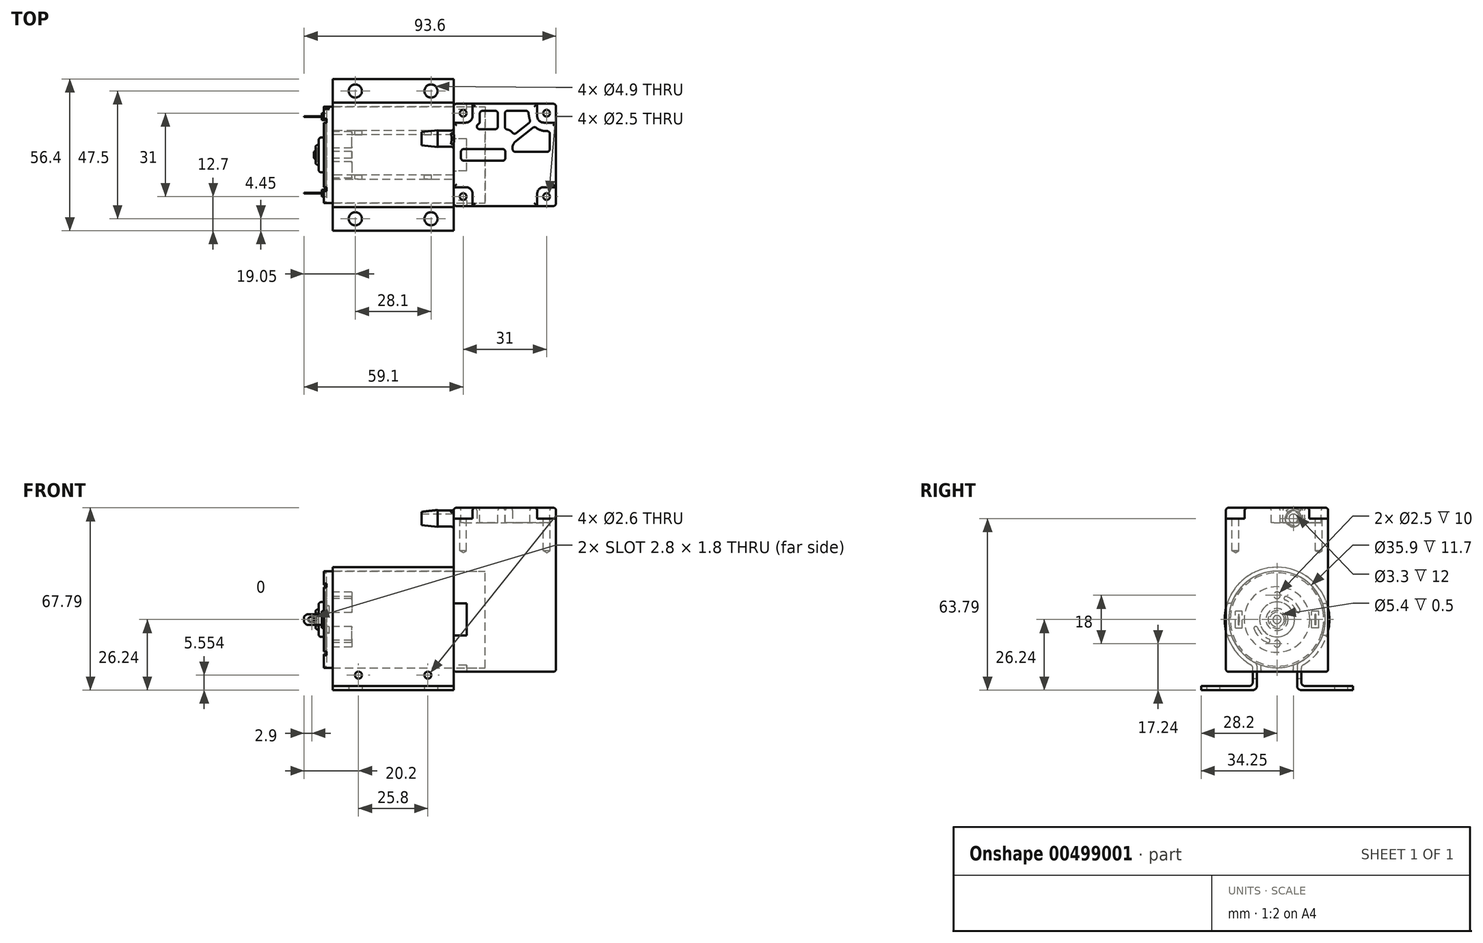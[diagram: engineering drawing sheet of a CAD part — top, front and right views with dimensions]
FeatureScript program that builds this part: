
annotation { "Feature Type Name" : "Feature", "Feature Type Description" : "" }
export const myFeature = defineFeature(function(context is Context, id is Id, definition is map)
    precondition{}
    {
        {
            var Q0;
            Q0=qCreatedBy(makeId("Front.planeOp"),FACE);
            var sketch = newSketch(context, id + "F0", { "sketchPlane" : qUnion([Q0])});
            skLineSegment(sketch, "E0", {"start": v(-59, 17.35) * mm, "end": v(-60, 17.35) * mm});
            skLineSegment(sketch, "E1", {"start": v(-60, 17.35) * mm, "end": v(-60, 17.95) * mm});
            skLineSegment(sketch, "E2", {"start": v(-60, 17.95) * mm, "end": v(0, 17.95) * mm});
            skLineSegment(sketch, "E3", {"start": v(0, 0) * mm, "end": v(0, 17.95) * mm});
            skLineSegment(sketch, "E4", {"start": v(0, 0) * mm, "end": v(-63.6, 0) * mm});
            skLineSegment(sketch, "E5", {"start": v(-61.9, 6.5) * mm, "end": v(-61.9, 4.1) * mm});
            skLineSegment(sketch, "E6", {"start": v(-63, 3.3) * mm, "end": v(-63, 2.7) * mm});
            skLineSegment(sketch, "E7", {"start": v(-63, 2.7) * mm, "end": v(-62.5, 2.7) * mm});
            skLineSegment(sketch, "E8", {"start": v(-62.5, 2.7) * mm, "end": v(-62.5, 1.5) * mm});
            skLineSegment(sketch, "E9", {"start": v(-62.5, 1.5) * mm, "end": v(-63.6, 1.5) * mm});
            skLineSegment(sketch, "E10", {"start": v(-63.6, 1.5) * mm, "end": v(-63.6, 0) * mm});
            skLineSegment(sketch, "E11", {"start": v(-61.9, 6.5) * mm, "end": v(-59.5, 6.5) * mm});
            skLineSegment(sketch, "E12", {"start": v(-59.5, 6.5) * mm, "end": v(-59.5, 12.2) * mm});
            skLineSegment(sketch, "E13", {"start": v(-59, 17.35) * mm, "end": v(-59, 12.2) * mm});
            skLineSegment(sketch, "E14", {"start": v(-59, 12.2) * mm, "end": v(-59.5, 12.2) * mm});
            skPoint(sketch, "E15", {"position": v(-61.9, 5.3) * mm});
            skLineSegment(sketch, "E16", {"start": v(-61.9, 4.1) * mm, "end": v(-63, 3.3) * mm});
            skSolve(sketch);
        }
        {
            var Q0;
            Q0 = qSketchRegion(id + "F0", true);
            var Q1;
            Q1=sQuery(id+"F0.wireOp",EDGE,"E4");
            revolve(context, id + "F1", {"entities" : qUnion([Q0]), "axis" : qUnion([Q1]), "revolveType" : RevolveType.FULL});
        }
        {
            var Q0;
            Q0=makeQuery(id+"F1.opRevolve","SWEPT_EDGE",EDGE,{"disambiguationData":[OSD([sQuery(id+"F0.wireOp",EDGE,"E12"),sQuery(id+"F0.wireOp",EDGE,"E14")])]});
            var Q1;
            Q1=makeQuery(id+"F1.opRevolve","SWEPT_EDGE",EDGE,{"disambiguationData":[OSD([sQuery(id+"F0.wireOp",EDGE,"E9"),sQuery(id+"F0.wireOp",EDGE,"E10")])]});
            fillet(context, id + "F2", {"entities" : qUnion([Q0, Q1]), "radius" : 0.5 * mm, "tangentPropagation" : true, "allowEdgeOverflow" : false});
        }
        {
            var Q0;
            Q0=makeQuery(id+"F1.opRevolve","SWEPT_EDGE",EDGE,{"disambiguationData":[OSD([sQuery(id+"F0.wireOp",EDGE,"E5"),sQuery(id+"F0.wireOp",EDGE,"E11")])]});
            fillet(context, id + "F3", {"entities" : qUnion([Q0]), "radius" : 1 * mm, "tangentPropagation" : true, "allowEdgeOverflow" : false});
        }
        {
            var Q0;
            Q0=makeQuery(id+"F1.opRevolve","SWEPT_FACE",FACE,{"disambiguationData":[OSD([sQuery(id+"F0.wireOp",EDGE,"E12")])]});
            var sketch = newSketch(context, id + "F4", { "sketchPlane" : qUnion([Q0])});
            skArc(sketch, "E17", {"start": v(-3.56, 8.54) * mm, "mid": v(-6.54, 6.54) * mm, "end": v(-8.54, 3.56) * mm});
            skArc(sketch, "E18", {"start": v(-3.02, 7.24) * mm, "mid": v(-5.55, 5.55) * mm, "end": v(-7.24, 3.02) * mm});
            skArc(sketch, "E19", {"start": v(-8.54, 3.56) * mm, "mid": v(-8.16, 2.65) * mm, "end": v(-7.24, 3.02) * mm});
            skArc(sketch, "E20", {"start": v(-3.02, 7.24) * mm, "mid": v(-2.65, 8.16) * mm, "end": v(-3.56, 8.54) * mm});
            skLineSegment(sketch, "E21", {"start": v(0, 9) * mm, "end": v(0, 0) * mm, "construction": true});
            skLineSegment(sketch, "E22", {"start": v(0, 0) * mm, "end": v(0, -9) * mm, "construction": true});
            skCircle(sketch, "E23", {"center": v(0, 9) * mm, "radius": 1.25 * mm});
            skCircle(sketch, "E24", {"center": v(0, -9) * mm, "radius": 1.25 * mm});
            skLineSegment(sketch, "E25", {"start": v(0, 0) * mm, "end": v(-9.9, 9.9) * mm, "construction": true});
            skArc(sketch, "E26.1.0", {"start": v(3.02, -7.24) * mm, "mid": v(5.55, -5.55) * mm, "end": v(7.24, -3.02) * mm});
            skArc(sketch, "E26.1.1", {"start": v(3.56, -8.54) * mm, "mid": v(6.54, -6.54) * mm, "end": v(8.54, -3.56) * mm});
            skArc(sketch, "E26.1.2", {"start": v(3.02, -7.24) * mm, "mid": v(2.65, -8.16) * mm, "end": v(3.56, -8.54) * mm});
            skArc(sketch, "E26.1.3", {"start": v(8.54, -3.56) * mm, "mid": v(8.16, -2.65) * mm, "end": v(7.24, -3.02) * mm});
            skSolve(sketch);
        }
        {
            var Q0;
            Q0=qSketchRegion(id+"F4",true);
            extrude(context, id + "F5", {"entities" : qUnion([Q0]), "operationType" : NewBodyOperationType.REMOVE, "oppositeDirection" : true, "depth" : 10 * mm});
        }
        {
            var Q0;
            Q0=makeQuery(id+"F1.opRevolve","SWEPT_FACE",FACE,{"disambiguationData":[OSD([sQuery(id+"F0.wireOp",EDGE,"E1")])]});
            var sketch = newSketch(context, id + "F6", { "sketchPlane" : qUnion([Q0])});
            skArc(sketch, "E27.0", {"start": v(-11.6, 12.9) * mm, "mid": v(-12.3, 12.24) * mm, "end": v(-12.96, 11.53) * mm});
            skArc(sketch, "E28.0", {"start": v(-12, 13.35) * mm, "mid": v(-12.73, 12.66) * mm, "end": v(-13.41, 11.93) * mm});
            skLineSegment(sketch, "E29", {"start": v(-13.41, 11.93) * mm, "end": v(-12.96, 11.53) * mm});
            skLineSegment(sketch, "E30", {"start": v(-12, 13.35) * mm, "end": v(-11.6, 12.9) * mm});
            skLineSegment(sketch, "E31.MirrorCS", {"start": v(12, 13.35) * mm, "end": v(11.6, 12.9) * mm});
            skLineSegment(sketch, "E32.MirrorCS", {"start": v(13.41, 11.93) * mm, "end": v(12.96, 11.53) * mm});
            skLineSegment(sketch, "E33.MirrorCS", {"start": v(-13.41, -11.93) * mm, "end": v(-12.96, -11.53) * mm});
            skLineSegment(sketch, "E34.MirrorCS", {"start": v(-12, -13.35) * mm, "end": v(-11.6, -12.9) * mm});
            skLineSegment(sketch, "E35.MirrorCS", {"start": v(13.41, -11.93) * mm, "end": v(12.96, -11.53) * mm});
            skLineSegment(sketch, "E36.MirrorCS", {"start": v(12, -13.35) * mm, "end": v(11.6, -12.9) * mm});
            skArc(sketch, "E37.trimOffspring", {"start": v(-12.96, -11.53) * mm, "mid": v(-12.3, -12.24) * mm, "end": v(-11.6, -12.9) * mm});
            skArc(sketch, "E38.trimOffspring", {"start": v(-13.41, -11.93) * mm, "mid": v(-12.73, -12.66) * mm, "end": v(-12, -13.35) * mm});
            skArc(sketch, "E39.trimOffspring", {"start": v(12.96, 11.53) * mm, "mid": v(12.3, 12.24) * mm, "end": v(11.6, 12.9) * mm});
            skArc(sketch, "E40.trimOffspring", {"start": v(13.41, 11.93) * mm, "mid": v(12.73, 12.66) * mm, "end": v(12, 13.35) * mm});
            skArc(sketch, "E41.trimOffspring", {"start": v(12, -13.35) * mm, "mid": v(12.73, -12.66) * mm, "end": v(13.41, -11.93) * mm});
            skArc(sketch, "E42.trimOffspring", {"start": v(11.6, -12.9) * mm, "mid": v(12.3, -12.24) * mm, "end": v(12.96, -11.53) * mm});
            skLineSegment(sketch, "E43", {"start": v(-17.92, 1) * mm, "end": v(-17.32, 0.97) * mm});
            skLineSegment(sketch, "E44", {"start": v(-17.92, -1) * mm, "end": v(-17.32, -0.97) * mm});
            skArc(sketch, "E45.0", {"start": v(-17.32, 0.97) * mm, "mid": v(-17.35, 0) * mm, "end": v(-17.32, -0.97) * mm});
            skArc(sketch, "E46.0", {"start": v(-17.92, 1) * mm, "mid": v(-17.95, 0) * mm, "end": v(-17.92, -1) * mm});
            skSolve(sketch);
        }
        {
            var Q0;
            Q0=qSketchRegion(id+"F6",true);
            var Q1;
            Q1=makeQuery(id+"F1.opRevolve","SWEPT_FACE",FACE,{"disambiguationData":[OSD([sQuery(id+"F0.wireOp",EDGE,"E13")])]});
            extrude(context, id + "F7", {"entities" : qUnion([Q0]), "operationType" : NewBodyOperationType.REMOVE, "endBound" : BoundingType.UP_TO_SURFACE, "oppositeDirection" : true, "endBoundEntityFace" : qUnion([Q1]), "depth" : 25 * mm});
        }
        {
            var Q0;
            Q0=makeQuery(id+"F7.boolean.opBoolean","SPLIT",FACE,{"disambiguationData":[TD([makeQuery(id+"F7.opExtrude","SWEPT_FACE",FACE,{"disambiguationData":[OSD([sQuery(id+"F6.wireOp",EDGE,"E32.MirrorCS")])]})])],"derivedFrom":makeQuery(id+"F1.opRevolve","SWEPT_FACE",FACE,{"disambiguationData":[OSD([sQuery(id+"F0.wireOp",EDGE,"E1")])]})});
            var sketch = newSketch(context, id + "F8", { "sketchPlane" : qUnion([Q0])});
            skLineSegment(sketch, "E47", {"start": v(-17.2, 5.13) * mm, "end": v(-16.63, 4.96) * mm});
            skLineSegment(sketch, "E48", {"start": v(-17.75, 2.7) * mm, "end": v(-17.15, 2.6) * mm});
            skArc(sketch, "E49.0", {"start": v(-17.15, 2.6) * mm, "mid": v(-16.93, 3.79) * mm, "end": v(-16.63, 4.96) * mm});
            skArc(sketch, "E50.0", {"start": v(-17.75, 2.7) * mm, "mid": v(-17.52, 3.92) * mm, "end": v(-17.2, 5.13) * mm});
            skPoint(sketch, "E51.orphan", {"position": v(-17.92, 1) * mm});
            skArc(sketch, "E52.MirrorCS", {"start": v(-17.15, -2.6) * mm, "mid": v(-16.93, -3.79) * mm, "end": v(-16.63, -4.96) * mm});
            skLineSegment(sketch, "E53.MirrorCS", {"start": v(-17.2, -5.13) * mm, "end": v(-16.63, -4.96) * mm});
            skArc(sketch, "E54.MirrorCS", {"start": v(-17.75, -2.7) * mm, "mid": v(-17.52, -3.92) * mm, "end": v(-17.2, -5.13) * mm});
            skLineSegment(sketch, "E55.MirrorCS", {"start": v(-17.75, -2.7) * mm, "end": v(-17.15, -2.6) * mm});
            skSolve(sketch);
        }
        {
            var Q0;
            Q0=qSketchRegion(id+"F8",true);
            extrude(context, id + "F9", {"entities" : qUnion([Q0]), "operationType" : NewBodyOperationType.REMOVE, "oppositeDirection" : true, "depth" : 2 * mm});
        }
        {
            var Q0;
            {var subQ0=sQuery(id+"F0.wireOp",EDGE,"E13");Q0=makeQuery(id+"F7.boolean.opBoolean","MERGE",FACE,{"derivedFrom":[makeQuery(id+"F1.opRevolve","SWEPT_FACE",FACE,{"disambiguationData":[OSD([subQ0])]}),makeQuery(id+"F7.opExtrude","CAP_FACE",FACE,{"disambiguationData":[OSD([subQ0]),ownerDisambiguation([makeQuery(id+"F6.imprint","IMPRINT",EDGE,{"derivedFrom":sQuery(id+"F6.wireOp",EDGE,"E27.0")})])],"isStart":false}),makeQuery(id+"F7.opExtrude","CAP_FACE",FACE,{"disambiguationData":[OSD([subQ0]),ownerDisambiguation([makeQuery(id+"F6.imprint","IMPRINT",EDGE,{"derivedFrom":sQuery(id+"F6.wireOp",EDGE,"E31.MirrorCS")})])],"isStart":false}),makeQuery(id+"F7.opExtrude","CAP_FACE",FACE,{"disambiguationData":[OSD([subQ0]),ownerDisambiguation([makeQuery(id+"F6.imprint","IMPRINT",EDGE,{"derivedFrom":sQuery(id+"F6.wireOp",EDGE,"E33.MirrorCS")})])],"isStart":false}),makeQuery(id+"F7.opExtrude","CAP_FACE",FACE,{"disambiguationData":[OSD([subQ0]),ownerDisambiguation([makeQuery(id+"F6.imprint","IMPRINT",EDGE,{"derivedFrom":sQuery(id+"F6.wireOp",EDGE,"E35.MirrorCS")})])],"isStart":false}),makeQuery(id+"F7.opExtrude","CAP_FACE",FACE,{"disambiguationData":[OSD([subQ0]),ownerDisambiguation([makeQuery(id+"F6.imprint","IMPRINT",EDGE,{"derivedFrom":sQuery(id+"F6.wireOp",EDGE,"E43")})])],"isStart":false})]});}
            var sketch = newSketch(context, id + "F10", { "sketchPlane" : qUnion([Q0])});
            skLineSegment(sketch, "E56.left", {"start": v(-12.9, -3.1) * mm, "end": v(-12.9, 3.1) * mm});
            skLineSegment(sketch, "E56.right", {"start": v(-15.5, -3.1) * mm, "end": v(-15.5, 3.1) * mm});
            skPoint(sketch, "E56.middle", {"position": v(-14.2, 0) * mm});
            skLineSegment(sketch, "E57.MirrorCS", {"start": v(12.9, -3.1) * mm, "end": v(12.9, 3.1) * mm});
            skLineSegment(sketch, "E58.MirrorCS", {"start": v(15.5, -3.1) * mm, "end": v(15.5, 3.1) * mm});
            skLineSegment(sketch, "E59", {"start": v(-15.5, 3.1) * mm, "end": v(-12.9, 3.1) * mm});
            skLineSegment(sketch, "E60", {"start": v(-15.5, -3.1) * mm, "end": v(-12.9, -3.1) * mm});
            skLineSegment(sketch, "E61", {"start": v(12.9, 3.1) * mm, "end": v(15.5, 3.1) * mm});
            skLineSegment(sketch, "E62", {"start": v(15.5, -3.1) * mm, "end": v(12.9, -3.1) * mm});
            skSolve(sketch);
        }
        {
            var Q0;
            Q0=qSketchRegion(id+"F10",true);
            extrude(context, id + "F11", {"entities" : qUnion([Q0]), "operationType" : NewBodyOperationType.ADD, "depth" : 1.7 * mm});
        }
        {
            var Q0;
            Q0=makeQuery(id+"F11.opExtrude","SWEPT_FACE",FACE,{"disambiguationData":[OSD([sQuery(id+"F10.wireOp",EDGE,"E56.right")])]});
            var Q1;
            Q1=makeQuery(id+"F11.opExtrude","SWEPT_FACE",FACE,{"disambiguationData":[OSD([sQuery(id+"F10.wireOp",EDGE,"E56.left")])]});
            cPlane(context, id + "F12", {"entities" : qUnion([Q0, Q1]), "cplaneType" : CPlaneType.MID_PLANE, "offset" : 25 * mm, "width" : 150 * mm, "height" : 150 * mm});
        }
        {
            var Q0;
            Q0=qCreatedBy(id+"F12.planeOp",FACE);
            var sketch = newSketch(context, id + "F13", { "sketchPlane" : qUnion([Q0])});
            skLineSegment(sketch, "E63", {"start": v(67.3, -2) * mm, "end": v(60.7, -2) * mm});
            skLineSegment(sketch, "E64", {"start": v(60.7, -2) * mm, "end": v(60.7, 2) * mm});
            skLineSegment(sketch, "E65", {"start": v(60.7, 2) * mm, "end": v(67.3, 2) * mm});
            skLineSegment(sketch, "E66", {"start": v(67.3, 2) * mm, "end": v(67.3, -2) * mm});
            skArc(sketch, "E67", {"start": v(64.9, -0.9) * mm, "mid": v(65.8, 0) * mm, "end": v(64.9, 0.9) * mm});
            skPoint(sketch, "E67.centerSnap0", {"position": v(60.7, 0) * mm});
            skArc(sketch, "E68", {"start": v(63.9, 0.9) * mm, "mid": v(63, 0) * mm, "end": v(63.9, -0.9) * mm});
            skLineSegment(sketch, "E69", {"start": v(64.9, 0.9) * mm, "end": v(63.9, 0.9) * mm});
            skLineSegment(sketch, "E70", {"start": v(64.9, -0.9) * mm, "end": v(63.9, -0.9) * mm});
            skSolve(sketch);
        }
        {
            var Q0;
            Q0=qSketchRegion(id+"F13",true);
            extrude(context, id + "F14", {"entities" : qUnion([Q0]), "endBound" : BoundingType.SYMMETRIC, "depth" : 0.3 * mm});
        }
        {
            var Q0;
            Q0=makeQuery(id+"F14.opExtrude","SWEPT_EDGE",EDGE,{"disambiguationData":[OSD([sQuery(id+"F13.wireOp",EDGE,"E65"),sQuery(id+"F13.wireOp",EDGE,"E66")])]});
            var Q1;
            Q1=makeQuery(id+"F14.opExtrude","SWEPT_EDGE",EDGE,{"disambiguationData":[OSD([sQuery(id+"F13.wireOp",EDGE,"E63"),sQuery(id+"F13.wireOp",EDGE,"E66")])]});
            chamfer(context, id + "F15", {"entities" : qUnion([Q0, Q1]), "width" : 1 * mm, "tangentPropagation" : true});
        }
        {
            var Q0;
            Q0=makeQuery(id+"F14.opExtrude","SWEPT_BODY",BODY,{"disambiguationData":[OSD([sQuery(id+"F13.wireOp",EDGE,"E63"),sQuery(id+"F13.wireOp",EDGE,"E64"),sQuery(id+"F13.wireOp",EDGE,"E65"),sQuery(id+"F13.wireOp",EDGE,"E66"),sQuery(id+"F13.wireOp",EDGE,"E67"),sQuery(id+"F13.wireOp",EDGE,"E68"),sQuery(id+"F13.wireOp",EDGE,"E69"),sQuery(id+"F13.wireOp",EDGE,"E70")])]});
            var Q1;
            Q1=qCreatedBy(makeId("Front.planeOp"),FACE);
            mirror(context, id + "F16", {"operationType" : NewBodyOperationType.ADD, "entities" : qUnion([Q0]), "mirrorPlane" : qUnion([Q1])});
        }
        {
            var Q0;
            Q0=makeQuery(id+"F7.boolean.opBoolean","SPLIT",FACE,{"disambiguationData":[TD([makeQuery(id+"F7.opExtrude","SWEPT_FACE",FACE,{"disambiguationData":[OSD([sQuery(id+"F6.wireOp",EDGE,"E30")])]})])],"derivedFrom":makeQuery(id+"F1.opRevolve","SWEPT_FACE",FACE,{"disambiguationData":[OSD([sQuery(id+"F0.wireOp",EDGE,"E1")])]})});
            cPlane(context, id + "F17", {"entities" : qUnion([Q0]), "cplaneType" : CPlaneType.OFFSET, "offset" : 3.3 * mm, "oppositeDirection" : true, "width" : 150 * mm, "height" : 150 * mm});
        }
        {
            var Q0;
            Q0=qCreatedBy(id+"F17.planeOp",FACE);
            var sketch = newSketch(context, id + "F18", { "sketchPlane" : qUnion([Q0])});
            skArc(sketch, "E71", {"start": v(7.5, -16.3) * mm, "mid": v(0, 17.95) * mm, "end": v(-7.5, -16.3) * mm});
            skLineSegment(sketch, "E72", {"start": v(-7.5, -16.3) * mm, "end": v(-7.5, -26.24) * mm});
            skLineSegment(sketch, "E73", {"start": v(-7.5, -26.24) * mm, "end": v(-28.2, -26.24) * mm});
            skLineSegment(sketch, "E74", {"start": v(-28.2, -26.24) * mm, "end": v(-28.2, -24.74) * mm});
            skLineSegment(sketch, "E75", {"start": v(-28.2, -24.74) * mm, "end": v(-9, -24.74) * mm});
            skLineSegment(sketch, "E76", {"start": v(-9, -24.74) * mm, "end": v(-9, -17.24) * mm});
            skLineSegment(sketch, "E77.MirrorCS", {"start": v(7.5, -16.3) * mm, "end": v(7.5, -26.24) * mm});
            skLineSegment(sketch, "E78.MirrorCS", {"start": v(9, -24.74) * mm, "end": v(9, -17.24) * mm});
            skLineSegment(sketch, "E79.MirrorCS", {"start": v(28.2, -24.74) * mm, "end": v(9, -24.74) * mm});
            skLineSegment(sketch, "E80.MirrorCS", {"start": v(7.5, -26.24) * mm, "end": v(28.2, -26.24) * mm});
            skLineSegment(sketch, "E81.MirrorCS", {"start": v(28.2, -26.24) * mm, "end": v(28.2, -24.74) * mm});
            skArc(sketch, "E82.trimOffspring", {"start": v(9, -17.24) * mm, "mid": v(0, 19.45) * mm, "end": v(-9, -17.24) * mm});
            skSolve(sketch);
        }
        {
            var Q0;
            Q0=makeQuery(id+"F18.imprint","IMPRINT",FACE,{"disambiguationData":[TD([[makeQuery(id+"F18.imprint","IMPRINT",EDGE,{"derivedFrom":sQuery(id+"F18.wireOp",EDGE,"E71")}),-1.0]])]});
            extrude(context, id + "F19", {"entities" : qUnion([Q0]), "oppositeDirection" : true, "depth" : 45 * mm});
        }
        {
            var Q0;
            Q0=makeQuery(id+"F19.opExtrude","SWEPT_EDGE",EDGE,{"disambiguationData":[OSD([sQuery(id+"F18.wireOp",EDGE,"E76"),sQuery(id+"F18.wireOp",EDGE,"E82.trimOffspring")])]});
            var Q1;
            Q1=makeQuery(id+"F19.opExtrude","SWEPT_EDGE",EDGE,{"disambiguationData":[OSD([sQuery(id+"F18.wireOp",EDGE,"E75"),sQuery(id+"F18.wireOp",EDGE,"E76")])]});
            var Q2;
            Q2=makeQuery(id+"F19.opExtrude","SWEPT_EDGE",EDGE,{"disambiguationData":[OSD([sQuery(id+"F18.wireOp",EDGE,"E72"),sQuery(id+"F18.wireOp",EDGE,"E73")])]});
            var Q3;
            Q3=makeQuery(id+"F19.opExtrude","SWEPT_EDGE",EDGE,{"disambiguationData":[OSD([sQuery(id+"F18.wireOp",EDGE,"E71"),sQuery(id+"F18.wireOp",EDGE,"E72")])]});
            var Q4;
            Q4=makeQuery(id+"F19.opExtrude","SWEPT_EDGE",EDGE,{"disambiguationData":[OSD([sQuery(id+"F18.wireOp",EDGE,"E71"),sQuery(id+"F18.wireOp",EDGE,"E77.MirrorCS")])]});
            var Q5;
            Q5=makeQuery(id+"F19.opExtrude","SWEPT_EDGE",EDGE,{"disambiguationData":[OSD([sQuery(id+"F18.wireOp",EDGE,"E77.MirrorCS"),sQuery(id+"F18.wireOp",EDGE,"E80.MirrorCS")])]});
            var Q6;
            Q6=makeQuery(id+"F19.opExtrude","SWEPT_EDGE",EDGE,{"disambiguationData":[OSD([sQuery(id+"F18.wireOp",EDGE,"E78.MirrorCS"),sQuery(id+"F18.wireOp",EDGE,"E79.MirrorCS")])]});
            var Q7;
            Q7=makeQuery(id+"F19.opExtrude","SWEPT_EDGE",EDGE,{"disambiguationData":[OSD([sQuery(id+"F18.wireOp",EDGE,"E78.MirrorCS"),sQuery(id+"F18.wireOp",EDGE,"E82.trimOffspring")])]});
            fillet(context, id + "F20", {"entities" : qUnion([Q0, Q1, Q2, Q3, Q4, Q5, Q6, Q7]), "radius" : 1.5 * mm, "tangentPropagation" : true, "allowEdgeOverflow" : false});
        }
        {
            var Q0;
            Q0=qCreatedBy(makeId("Front.planeOp"),FACE);
            var sketch = newSketch(context, id + "F21", { "sketchPlane" : qUnion([Q0])});
            skLineSegment(sketch, "E83.bottom", {"start": v(-11.7, 41.55) * mm, "end": v(26.3, 41.55) * mm});
            skLineSegment(sketch, "E83.top", {"start": v(-11.7, -19.45) * mm, "end": v(26.3, -19.45) * mm});
            skLineSegment(sketch, "E83.left", {"start": v(-11.7, 41.55) * mm, "end": v(-11.7, -19.45) * mm});
            skLineSegment(sketch, "E83.right", {"start": v(26.3, 41.55) * mm, "end": v(26.3, -19.45) * mm});
            skLineSegment(sketch, "E84", {"start": v(0, -17.95) * mm, "end": v(-60, -17.95) * mm, "construction": true});
            skLineSegment(sketch, "E85", {"start": v(-60, 17.95) * mm, "end": v(0, 17.95) * mm, "construction": true});
            skSolve(sketch);
        }
        {
            var Q0;
            Q0=makeQuery(id+"F21.imprint","IMPRINT",FACE,{"disambiguationData":[TD([[makeQuery(id+"F21.imprint","IMPRINT",EDGE,{"derivedFrom":sQuery(id+"F21.wireOp",EDGE,"E83.bottom")}),-1.0]])]});
            extrude(context, id + "F22", {"entities" : qUnion([Q0]), "endBound" : BoundingType.SYMMETRIC, "depth" : 38 * mm});
        }
        {
            var Q0;
            Q0=makeQuery(id+"F1.opRevolve","SWEPT_BODY",BODY,{"disambiguationData":[OSD([sQuery(id+"F0.wireOp",EDGE,"E0"),sQuery(id+"F0.wireOp",EDGE,"E1"),sQuery(id+"F0.wireOp",EDGE,"E2"),sQuery(id+"F0.wireOp",EDGE,"E3"),sQuery(id+"F0.wireOp",EDGE,"E4"),sQuery(id+"F0.wireOp",EDGE,"E5"),sQuery(id+"F0.wireOp",EDGE,"E6"),sQuery(id+"F0.wireOp",EDGE,"E7"),sQuery(id+"F0.wireOp",EDGE,"E8"),sQuery(id+"F0.wireOp",EDGE,"E9"),sQuery(id+"F0.wireOp",EDGE,"E10"),sQuery(id+"F0.wireOp",EDGE,"E11"),sQuery(id+"F0.wireOp",EDGE,"E12"),sQuery(id+"F0.wireOp",EDGE,"E13"),sQuery(id+"F0.wireOp",EDGE,"E14"),sQuery(id+"F0.wireOp",EDGE,"E16")])]});
            var Q1;
            Q1=makeQuery(id+"F22.opExtrude","SWEPT_BODY",BODY,{"disambiguationData":[OSD([sQuery(id+"F21.wireOp",EDGE,"E83.bottom"),sQuery(id+"F21.wireOp",EDGE,"E83.top"),sQuery(id+"F21.wireOp",EDGE,"E83.left"),sQuery(id+"F21.wireOp",EDGE,"E83.right")])]});
            booleanBodies(context, id + "F23", {"operationType" : BooleanOperationType.SUBTRACTION, "tools" : qUnion([Q0]), "targets" : qUnion([Q1]), "keepTools" : true});
        }
        {
            var Q0;
            Q0=makeQuery(id+"F22.opExtrude","SWEPT_FACE",FACE,{"disambiguationData":[OSD([sQuery(id+"F21.wireOp",EDGE,"E83.left")])]});
            var sketch = newSketch(context, id + "F24", { "sketchPlane" : qUnion([Q0])});
            skArc(sketch, "E86", {"start": v(-16.94, -5.95) * mm, "mid": v(-17.95, 0) * mm, "end": v(-16.94, 5.95) * mm});
            skLineSegment(sketch, "E87", {"start": v(-16.94, 5.95) * mm, "end": v(-19, 5.95) * mm});
            skLineSegment(sketch, "E88", {"start": v(-19, 5.95) * mm, "end": v(-19, -5.95) * mm});
            skLineSegment(sketch, "E89", {"start": v(-19, -5.95) * mm, "end": v(-16.94, -5.95) * mm});
            skLineSegment(sketch, "E90.MirrorCS", {"start": v(16.94, 5.95) * mm, "end": v(19, 5.95) * mm});
            skLineSegment(sketch, "E91.MirrorCS", {"start": v(19, 5.95) * mm, "end": v(19, -5.95) * mm});
            skLineSegment(sketch, "E92.MirrorCS", {"start": v(19, -5.95) * mm, "end": v(16.94, -5.95) * mm});
            skArc(sketch, "E93.MirrorCS", {"start": v(16.94, -5.95) * mm, "mid": v(17.95, 0) * mm, "end": v(16.94, 5.95) * mm});
            skLineSegment(sketch, "E94", {"start": v(-5.95, -16.94) * mm, "end": v(-5.95, -19.45) * mm});
            skLineSegment(sketch, "E95", {"start": v(-5.95, -19.45) * mm, "end": v(5.95, -19.45) * mm});
            skLineSegment(sketch, "E96", {"start": v(5.95, -19.45) * mm, "end": v(5.95, -16.94) * mm});
            skArc(sketch, "E97.trimOffspring", {"start": v(5.95, -16.94) * mm, "mid": v(0, -17.95) * mm, "end": v(-5.95, -16.94) * mm});
            skSolve(sketch);
        }
        {
            var Q0;
            Q0=makeQuery(id+"F24.imprint","IMPRINT",FACE,{"disambiguationData":[TD([[makeQuery(id+"F24.imprint","IMPRINT",EDGE,{"derivedFrom":sQuery(id+"F24.wireOp",EDGE,"E90.MirrorCS")}),-1.0]])]});
            var Q1;
            Q1=makeQuery(id+"F24.imprint","IMPRINT",FACE,{"disambiguationData":[TD([[makeQuery(id+"F24.imprint","IMPRINT",EDGE,{"derivedFrom":sQuery(id+"F24.wireOp",EDGE,"E86")}),-1.0]])]});
            var Q2;
            Q2=makeQuery(id+"F24.imprint","IMPRINT",FACE,{"disambiguationData":[TD([[makeQuery(id+"F24.imprint","IMPRINT",EDGE,{"derivedFrom":sQuery(id+"F24.wireOp",EDGE,"E94")}),1.0]])]});
            extrude(context, id + "F25", {"entities" : qUnion([Q0, Q1, Q2]), "operationType" : NewBodyOperationType.REMOVE, "oppositeDirection" : true, "depth" : 4.8 * mm});
        }
        {
            var Q0;
            Q0=makeQuery(id+"F22.opExtrude","SWEPT_FACE",FACE,{"disambiguationData":[OSD([sQuery(id+"F21.wireOp",EDGE,"E83.bottom")])]});
            var sketch = newSketch(context, id + "F26", { "sketchPlane" : qUnion([Q0])});
            skLineSegment(sketch, "E98.bottom", {"start": v(26.3, 19) * mm, "end": v(19.3, 19) * mm});
            skLineSegment(sketch, "E98.top", {"start": v(26.3, 12) * mm, "end": v(19.3, 12) * mm});
            skLineSegment(sketch, "E98.left", {"start": v(26.3, 19) * mm, "end": v(26.3, 12) * mm});
            skLineSegment(sketch, "E98.right", {"start": v(19.3, 19) * mm, "end": v(19.3, 12) * mm});
            skLineSegment(sketch, "E99.bottom", {"start": v(26.3, -19) * mm, "end": v(19.3, -19) * mm});
            skLineSegment(sketch, "E99.top", {"start": v(26.3, -12) * mm, "end": v(19.3, -12) * mm});
            skLineSegment(sketch, "E99.left", {"start": v(26.3, -19) * mm, "end": v(26.3, -12) * mm});
            skLineSegment(sketch, "E99.right", {"start": v(19.3, -19) * mm, "end": v(19.3, -12) * mm});
            skLineSegment(sketch, "E100.bottom", {"start": v(-11.7, -19) * mm, "end": v(-4.7, -19) * mm});
            skLineSegment(sketch, "E100.top", {"start": v(-11.7, -12) * mm, "end": v(-4.7, -12) * mm});
            skLineSegment(sketch, "E100.left", {"start": v(-11.7, -19) * mm, "end": v(-11.7, -12) * mm});
            skLineSegment(sketch, "E100.right", {"start": v(-4.7, -19) * mm, "end": v(-4.7, -12) * mm});
            skLineSegment(sketch, "E101.bottom", {"start": v(-11.7, 19) * mm, "end": v(-4.7, 19) * mm});
            skLineSegment(sketch, "E101.top", {"start": v(-11.7, 12) * mm, "end": v(-4.7, 12) * mm});
            skLineSegment(sketch, "E101.left", {"start": v(-11.7, 19) * mm, "end": v(-11.7, 12) * mm});
            skLineSegment(sketch, "E101.right", {"start": v(-4.7, 19) * mm, "end": v(-4.7, 12) * mm});
            skSolve(sketch);
        }
        {
            var Q0;
            Q0=makeQuery(id+"F26.imprint","IMPRINT",FACE,{"disambiguationData":[TD([[makeQuery(id+"F26.imprint","IMPRINT",EDGE,{"derivedFrom":sQuery(id+"F26.wireOp",EDGE,"E101.bottom")}),-1.0]])]});
            var Q1;
            Q1=makeQuery(id+"F26.imprint","IMPRINT",FACE,{"disambiguationData":[TD([[makeQuery(id+"F26.imprint","IMPRINT",EDGE,{"derivedFrom":sQuery(id+"F26.wireOp",EDGE,"E98.bottom")}),-1.0]])]});
            var Q2;
            Q2=makeQuery(id+"F26.imprint","IMPRINT",FACE,{"disambiguationData":[TD([[makeQuery(id+"F26.imprint","IMPRINT",EDGE,{"derivedFrom":sQuery(id+"F26.wireOp",EDGE,"E99.bottom")}),1.0]])]});
            var Q3;
            Q3=makeQuery(id+"F26.imprint","IMPRINT",FACE,{"disambiguationData":[TD([[makeQuery(id+"F26.imprint","IMPRINT",EDGE,{"derivedFrom":sQuery(id+"F26.wireOp",EDGE,"E100.bottom")}),1.0]])]});
            extrude(context, id + "F27", {"entities" : qUnion([Q0, Q1, Q2, Q3]), "operationType" : NewBodyOperationType.REMOVE, "oppositeDirection" : true, "depth" : 4 * mm});
        }
        {
            var Q0;
            Q0=makeQuery(id+"F27.boolean.opBoolean","COPY",EDGE,{"derivedFrom":makeQuery(id+"F27.opExtrude","SWEPT_EDGE",EDGE,{"disambiguationData":[OSD([sQuery(id+"F26.wireOp",EDGE,"E100.top"),sQuery(id+"F26.wireOp",EDGE,"E100.right")])]})});
            var Q1;
            Q1=makeQuery(id+"F27.boolean.opBoolean","COPY",EDGE,{"derivedFrom":makeQuery(id+"F27.opExtrude","SWEPT_EDGE",EDGE,{"disambiguationData":[OSD([sQuery(id+"F26.wireOp",EDGE,"E99.top"),sQuery(id+"F26.wireOp",EDGE,"E99.right")])]})});
            var Q2;
            Q2=makeQuery(id+"F27.boolean.opBoolean","COPY",EDGE,{"derivedFrom":makeQuery(id+"F27.opExtrude","SWEPT_EDGE",EDGE,{"disambiguationData":[OSD([sQuery(id+"F26.wireOp",EDGE,"E98.top"),sQuery(id+"F26.wireOp",EDGE,"E98.right")])]})});
            var Q3;
            Q3=makeQuery(id+"F27.boolean.opBoolean","COPY",EDGE,{"derivedFrom":makeQuery(id+"F27.opExtrude","SWEPT_EDGE",EDGE,{"disambiguationData":[OSD([sQuery(id+"F26.wireOp",EDGE,"E101.top"),sQuery(id+"F26.wireOp",EDGE,"E101.right")])]})});
            fillet(context, id + "F28", {"entities" : qUnion([Q0, Q1, Q2, Q3]), "radius" : 2.5 * mm, "tangentPropagation" : true, "allowEdgeOverflow" : false});
        }
        {
            var Q0;
            Q0=makeQuery(id+"F27.boolean.opBoolean","COPY",FACE,{"derivedFrom":makeQuery(id+"F27.opExtrude","CAP_FACE",FACE,{"disambiguationData":[OSD([sQuery(id+"F26.wireOp",EDGE,"E99.bottom"),sQuery(id+"F26.wireOp",EDGE,"E99.top"),sQuery(id+"F26.wireOp",EDGE,"E99.left"),sQuery(id+"F26.wireOp",EDGE,"E99.right")])],"isStart":false})});
            var sketch = newSketch(context, id + "F29", { "sketchPlane" : qUnion([Q0])});
            skPoint(sketch, "E102", {"position": v(22.8, 15.5) * mm});
            skPoint(sketch, "E103", {"position": v(22.8, -15.5) * mm});
            skPoint(sketch, "E104", {"position": v(-8.2, -15.5) * mm});
            skPoint(sketch, "E105", {"position": v(-8.2, 15.5) * mm});
            skSolve(sketch);
        }
        {
            var Q0;
            Q0=sQuery(id+"F29.wireOp",VERTEX,"E105");
            var Q1;
            Q1=sQuery(id+"F29.wireOp",VERTEX,"E102");
            var Q2;
            Q2=sQuery(id+"F29.wireOp",VERTEX,"E103");
            var Q3;
            Q3=sQuery(id+"F29.wireOp",VERTEX,"E104");
            var Q4;
            Q4=makeQuery(id+"F22.opExtrude","SWEPT_BODY",BODY,{"disambiguationData":[OSD([sQuery(id+"F21.wireOp",EDGE,"E83.bottom"),sQuery(id+"F21.wireOp",EDGE,"E83.top"),sQuery(id+"F21.wireOp",EDGE,"E83.left"),sQuery(id+"F21.wireOp",EDGE,"E83.right")])]});
            hole(context, id + "F30", {"style" : HoleStyle.SIMPLE, "endStyle" : HoleEndStyle.BLIND, "holeDiameter" : 2.5 * mm, "holeDepth" : 12 * mm, "isTappedThrough" : true, "tappedDepth" : 12 * mm, "tapClearance" : 3, "locations" : qUnion([Q0, Q1, Q2, Q3]), "scope" : qUnion([Q4])});
        }
        {
            var Q0;
            Q0=makeQuery(id+"F22.opExtrude","SWEPT_FACE",FACE,{"disambiguationData":[OSD([sQuery(id+"F21.wireOp",EDGE,"E83.bottom")])]});
            var sketch = newSketch(context, id + "F31", { "sketchPlane" : qUnion([Q0])});
            skLineSegment(sketch, "E106", {"start": v(24, 8.96) * mm, "end": v(24, 1.15) * mm});
            skLineSegment(sketch, "E107", {"start": v(24, 1.15) * mm, "end": v(10.2, 1.15) * mm});
            skLineSegment(sketch, "E108", {"start": v(10.2, 1.15) * mm, "end": v(10.2, 3.54) * mm});
            skArc(sketch, "E109", {"start": v(16.2, 16.4) * mm, "mid": v(16.25, 14.36) * mm, "end": v(16.9, 12.42) * mm});
            skArc(sketch, "E110", {"start": v(10.67, 7.4) * mm, "mid": v(9.3, 8.97) * mm, "end": v(7.3, 9.55) * mm});
            skLineSegment(sketch, "E111", {"start": v(10.76, 4.52) * mm, "end": v(18.3, 10.6) * mm});
            skLineSegment(sketch, "E112", {"start": v(16.9, 12.42) * mm, "end": v(10.67, 7.4) * mm});
            skLineSegment(sketch, "E113", {"start": v(16.2, 16.4) * mm, "end": v(7.3, 16.4) * mm});
            skLineSegment(sketch, "E114", {"start": v(7.3, 16.4) * mm, "end": v(7.3, 9.55) * mm});
            skLineSegment(sketch, "E115", {"start": v(-2, 16.4) * mm, "end": v(4.7, 16.4) * mm});
            skLineSegment(sketch, "E116", {"start": v(4.7, 16.4) * mm, "end": v(4.7, 9.55) * mm});
            skLineSegment(sketch, "E117", {"start": v(4.7, 9.55) * mm, "end": v(-5.3, 9.55) * mm});
            skLineSegment(sketch, "E118", {"start": v(-5.3, 9.55) * mm, "end": v(-2, 11.82) * mm});
            skLineSegment(sketch, "E119", {"start": v(-2, 11.82) * mm, "end": v(-2, 16.4) * mm});
            skLineSegment(sketch, "E120.bottom", {"start": v(-9, -2.15) * mm, "end": v(7.5, -2.15) * mm});
            skLineSegment(sketch, "E120.top", {"start": v(-9, 2.15) * mm, "end": v(7.5, 2.15) * mm});
            skLineSegment(sketch, "E120.left", {"start": v(-9, -2.15) * mm, "end": v(-9, 2.15) * mm});
            skLineSegment(sketch, "E120.right", {"start": v(7.5, -2.15) * mm, "end": v(7.5, 2.15) * mm});
            skPoint(sketch, "E120.middle", {"position": v(-0.75, 0) * mm});
            skArc(sketch, "E121.trimOffspring", {"start": v(18.3, 10.6) * mm, "mid": v(20.96, 9.1) * mm, "end": v(24, 8.96) * mm});
            skArc(sketch, "E122.trimOffspring", {"start": v(10.2, 3.54) * mm, "mid": v(10.52, 4.01) * mm, "end": v(10.76, 4.52) * mm});
            skSolve(sketch);
        }
        {
            var Q0;
            Q0=makeQuery(id+"F31.imprint","IMPRINT",FACE,{"disambiguationData":[TD([[makeQuery(id+"F31.imprint","IMPRINT",EDGE,{"derivedFrom":sQuery(id+"F31.wireOp",EDGE,"E109")}),-1.0]])]});
            var Q1;
            Q1=makeQuery(id+"F31.imprint","IMPRINT",FACE,{"disambiguationData":[TD([[makeQuery(id+"F31.imprint","IMPRINT",EDGE,{"derivedFrom":sQuery(id+"F31.wireOp",EDGE,"E106")}),-1.0]])]});
            var Q2;
            Q2=makeQuery(id+"F31.imprint","IMPRINT",FACE,{"disambiguationData":[TD([[makeQuery(id+"F31.imprint","IMPRINT",EDGE,{"derivedFrom":sQuery(id+"F31.wireOp",EDGE,"E115")}),-1.0]])]});
            var Q3;
            Q3=makeQuery(id+"F31.imprint","IMPRINT",FACE,{"disambiguationData":[TD([[makeQuery(id+"F31.imprint","IMPRINT",EDGE,{"derivedFrom":sQuery(id+"F31.wireOp",EDGE,"E120.bottom")}),1.0]])]});
            extrude(context, id + "F32", {"entities" : qUnion([Q0, Q1, Q2, Q3]), "operationType" : NewBodyOperationType.REMOVE, "oppositeDirection" : true, "depth" : 5.6 * mm});
        }
        {
            var Q0;
            Q0=makeQuery(id+"F32.boolean.opBoolean","COPY",EDGE,{"derivedFrom":makeQuery(id+"F32.opExtrude","SWEPT_EDGE",EDGE,{"disambiguationData":[OSD([sQuery(id+"F31.wireOp",EDGE,"E109"),sQuery(id+"F31.wireOp",EDGE,"E113")])]})});
            var Q1;
            Q1=makeQuery(id+"F32.boolean.opBoolean","COPY",EDGE,{"derivedFrom":makeQuery(id+"F32.opExtrude","SWEPT_EDGE",EDGE,{"disambiguationData":[OSD([sQuery(id+"F31.wireOp",EDGE,"E106"),sQuery(id+"F31.wireOp",EDGE,"E121.trimOffspring")])]})});
            var Q2;
            Q2=makeQuery(id+"F32.boolean.opBoolean","COPY",EDGE,{"derivedFrom":makeQuery(id+"F32.opExtrude","SWEPT_EDGE",EDGE,{"disambiguationData":[OSD([sQuery(id+"F31.wireOp",EDGE,"E115"),sQuery(id+"F31.wireOp",EDGE,"E116")])]})});
            var Q3;
            Q3=makeQuery(id+"F32.boolean.opBoolean","COPY",EDGE,{"derivedFrom":makeQuery(id+"F32.opExtrude","SWEPT_EDGE",EDGE,{"disambiguationData":[OSD([sQuery(id+"F31.wireOp",EDGE,"E120.top"),sQuery(id+"F31.wireOp",EDGE,"E120.right")])]})});
            var Q4;
            Q4=makeQuery(id+"F32.boolean.opBoolean","COPY",EDGE,{"derivedFrom":makeQuery(id+"F32.opExtrude","SWEPT_EDGE",EDGE,{"disambiguationData":[OSD([sQuery(id+"F31.wireOp",EDGE,"E109"),sQuery(id+"F31.wireOp",EDGE,"E112")])]})});
            var Q5;
            Q5=makeQuery(id+"F32.boolean.opBoolean","COPY",EDGE,{"derivedFrom":makeQuery(id+"F32.opExtrude","SWEPT_EDGE",EDGE,{"disambiguationData":[OSD([sQuery(id+"F31.wireOp",EDGE,"E106"),sQuery(id+"F31.wireOp",EDGE,"E107")])]})});
            var Q6;
            Q6=makeQuery(id+"F32.boolean.opBoolean","COPY",EDGE,{"derivedFrom":makeQuery(id+"F32.opExtrude","SWEPT_EDGE",EDGE,{"disambiguationData":[OSD([sQuery(id+"F31.wireOp",EDGE,"E120.bottom"),sQuery(id+"F31.wireOp",EDGE,"E120.right")])]})});
            var Q7;
            Q7=makeQuery(id+"F32.boolean.opBoolean","COPY",EDGE,{"derivedFrom":makeQuery(id+"F32.opExtrude","SWEPT_EDGE",EDGE,{"disambiguationData":[OSD([sQuery(id+"F31.wireOp",EDGE,"E116"),sQuery(id+"F31.wireOp",EDGE,"E117")])]})});
            var Q8;
            Q8=makeQuery(id+"F32.boolean.opBoolean","COPY",EDGE,{"derivedFrom":makeQuery(id+"F32.opExtrude","SWEPT_EDGE",EDGE,{"disambiguationData":[OSD([sQuery(id+"F31.wireOp",EDGE,"E107"),sQuery(id+"F31.wireOp",EDGE,"E108")])]})});
            var Q9;
            Q9=makeQuery(id+"F32.boolean.opBoolean","COPY",EDGE,{"derivedFrom":makeQuery(id+"F32.opExtrude","SWEPT_EDGE",EDGE,{"disambiguationData":[OSD([sQuery(id+"F31.wireOp",EDGE,"E120.bottom"),sQuery(id+"F31.wireOp",EDGE,"E120.left")])]})});
            var Q10;
            Q10=makeQuery(id+"F32.boolean.opBoolean","COPY",EDGE,{"derivedFrom":makeQuery(id+"F32.opExtrude","SWEPT_EDGE",EDGE,{"disambiguationData":[OSD([sQuery(id+"F31.wireOp",EDGE,"E110"),sQuery(id+"F31.wireOp",EDGE,"E114")])]})});
            var Q11;
            Q11=makeQuery(id+"F32.boolean.opBoolean","COPY",EDGE,{"derivedFrom":makeQuery(id+"F32.opExtrude","SWEPT_EDGE",EDGE,{"disambiguationData":[OSD([sQuery(id+"F31.wireOp",EDGE,"E117"),sQuery(id+"F31.wireOp",EDGE,"E118")])]})});
            var Q12;
            Q12=makeQuery(id+"F32.boolean.opBoolean","COPY",EDGE,{"derivedFrom":makeQuery(id+"F32.opExtrude","SWEPT_EDGE",EDGE,{"disambiguationData":[OSD([sQuery(id+"F31.wireOp",EDGE,"E118"),sQuery(id+"F31.wireOp",EDGE,"E119")])]})});
            var Q13;
            Q13=makeQuery(id+"F32.boolean.opBoolean","COPY",EDGE,{"derivedFrom":makeQuery(id+"F32.opExtrude","SWEPT_EDGE",EDGE,{"disambiguationData":[OSD([sQuery(id+"F31.wireOp",EDGE,"E120.top"),sQuery(id+"F31.wireOp",EDGE,"E120.left")])]})});
            var Q14;
            Q14=makeQuery(id+"F32.boolean.opBoolean","COPY",EDGE,{"derivedFrom":makeQuery(id+"F32.opExtrude","SWEPT_EDGE",EDGE,{"disambiguationData":[OSD([sQuery(id+"F31.wireOp",EDGE,"E115"),sQuery(id+"F31.wireOp",EDGE,"E119")])]})});
            var Q15;
            Q15=makeQuery(id+"F32.boolean.opBoolean","COPY",EDGE,{"derivedFrom":makeQuery(id+"F32.opExtrude","SWEPT_EDGE",EDGE,{"disambiguationData":[OSD([sQuery(id+"F31.wireOp",EDGE,"E113"),sQuery(id+"F31.wireOp",EDGE,"E114")])]})});
            var Q16;
            Q16=makeQuery(id+"F32.boolean.opBoolean","COPY",EDGE,{"derivedFrom":makeQuery(id+"F32.opExtrude","SWEPT_EDGE",EDGE,{"disambiguationData":[OSD([sQuery(id+"F31.wireOp",EDGE,"E111"),sQuery(id+"F31.wireOp",EDGE,"E121.trimOffspring")])]})});
            var Q17;
            Q17=makeQuery(id+"F32.boolean.opBoolean","COPY",EDGE,{"derivedFrom":makeQuery(id+"F32.opExtrude","SWEPT_EDGE",EDGE,{"disambiguationData":[OSD([sQuery(id+"F31.wireOp",EDGE,"E111"),sQuery(id+"F31.wireOp",EDGE,"E122.trimOffspring")])]})});
            var Q18;
            Q18=makeQuery(id+"F32.boolean.opBoolean","COPY",EDGE,{"derivedFrom":makeQuery(id+"F32.opExtrude","SWEPT_EDGE",EDGE,{"disambiguationData":[OSD([sQuery(id+"F31.wireOp",EDGE,"E108"),sQuery(id+"F31.wireOp",EDGE,"E122.trimOffspring")])]})});
            var Q19;
            Q19=makeQuery(id+"F32.boolean.opBoolean","COPY",EDGE,{"derivedFrom":makeQuery(id+"F32.opExtrude","SWEPT_EDGE",EDGE,{"disambiguationData":[OSD([sQuery(id+"F31.wireOp",EDGE,"E110"),sQuery(id+"F31.wireOp",EDGE,"E112")])]})});
            fillet(context, id + "F33", {"entities" : qUnion([Q0, Q1, Q2, Q3, Q4, Q5, Q6, Q7, Q8, Q9, Q10, Q11, Q12, Q13, Q14, Q15, Q16, Q17, Q18, Q19]), "radius" : 1 * mm, "tangentPropagation" : true, "allowEdgeOverflow" : false});
        }
        {
            var Q0;
            Q0=makeQuery(id+"F22.opExtrude","SWEPT_FACE",FACE,{"disambiguationData":[OSD([sQuery(id+"F21.wireOp",EDGE,"E83.bottom")])]});
            fillet(context, id + "F34", {"entities" : qUnion([Q0]), "radius" : 1 * mm, "tangentPropagation" : true, "allowEdgeOverflow" : false});
        }
        {
            var Q0;
            {var subQ0=sQuery(id+"F21.wireOp",EDGE,"E83.bottom");var subQ1=sQuery(id+"F21.wireOp",EDGE,"E83.left");Q0=makeQuery(id+"F25.boolean.opBoolean","SPLIT",EDGE,{"disambiguationData":[TD([makeQuery(id+"F22.opExtrude","SWEPT_FACE",FACE,{"disambiguationData":[OSD([subQ0])]})])],"derivedFrom":makeQuery(id+"F22.opExtrude","CAP_EDGE",EDGE,{"disambiguationData":[OSD([subQ1])],"isStart":true})});}
            var Q1;
            {var subQ0=sQuery(id+"F21.wireOp",EDGE,"E83.bottom");var subQ1=sQuery(id+"F21.wireOp",EDGE,"E83.left");Q1=makeQuery(id+"F25.boolean.opBoolean","SPLIT",EDGE,{"disambiguationData":[TD([makeQuery(id+"F22.opExtrude","SWEPT_FACE",FACE,{"disambiguationData":[OSD([subQ0])]})])],"derivedFrom":makeQuery(id+"F22.opExtrude","CAP_EDGE",EDGE,{"disambiguationData":[OSD([subQ1])],"isStart":false})});}
            var Q2;
            Q2=makeQuery(id+"F27.boolean.opBoolean","COPY",EDGE,{"derivedFrom":makeQuery(id+"F27.opExtrude","CAP_EDGE",EDGE,{"disambiguationData":[OSD([sQuery(id+"F26.wireOp",EDGE,"E100.left")])],"isStart":false})});
            var Q3;
            Q3=makeQuery(id+"F27.boolean.opBoolean","COPY",EDGE,{"derivedFrom":makeQuery(id+"F27.opExtrude","CAP_EDGE",EDGE,{"disambiguationData":[OSD([sQuery(id+"F26.wireOp",EDGE,"E100.bottom")])],"isStart":false})});
            var Q4;
            Q4=makeQuery(id+"F27.boolean.opBoolean","COPY",EDGE,{"derivedFrom":makeQuery(id+"F27.opExtrude","CAP_EDGE",EDGE,{"disambiguationData":[OSD([sQuery(id+"F26.wireOp",EDGE,"E101.left")])],"isStart":false})});
            var Q5;
            Q5=makeQuery(id+"F27.boolean.opBoolean","COPY",EDGE,{"derivedFrom":makeQuery(id+"F27.opExtrude","CAP_EDGE",EDGE,{"disambiguationData":[OSD([sQuery(id+"F26.wireOp",EDGE,"E101.bottom")])],"isStart":false})});
            var Q6;
            Q6=makeQuery(id+"F22.opExtrude","CAP_EDGE",EDGE,{"disambiguationData":[OSD([sQuery(id+"F21.wireOp",EDGE,"E83.right")])],"isStart":true});
            var Q7;
            Q7=makeQuery(id+"F27.boolean.opBoolean","COPY",EDGE,{"derivedFrom":makeQuery(id+"F27.opExtrude","CAP_EDGE",EDGE,{"disambiguationData":[OSD([sQuery(id+"F26.wireOp",EDGE,"E98.bottom")])],"isStart":false})});
            var Q8;
            Q8=makeQuery(id+"F27.boolean.opBoolean","COPY",EDGE,{"derivedFrom":makeQuery(id+"F27.opExtrude","CAP_EDGE",EDGE,{"disambiguationData":[OSD([sQuery(id+"F26.wireOp",EDGE,"E98.left")])],"isStart":false})});
            var Q9;
            Q9=makeQuery(id+"F27.boolean.opBoolean","COPY",EDGE,{"derivedFrom":makeQuery(id+"F27.opExtrude","CAP_EDGE",EDGE,{"disambiguationData":[OSD([sQuery(id+"F26.wireOp",EDGE,"E99.left")])],"isStart":false})});
            var Q10;
            Q10=makeQuery(id+"F27.boolean.opBoolean","COPY",EDGE,{"derivedFrom":makeQuery(id+"F27.opExtrude","SWEPT_EDGE",EDGE,{"disambiguationData":[OSD([sQuery(id+"F21.wireOp",EDGE,"E83.bottom"),sQuery(id+"F21.wireOp",EDGE,"E83.right"),sQuery(id+"F26.wireOp",EDGE,"E98.top"),sQuery(id+"F26.wireOp",EDGE,"E98.left")])]})});
            var Q11;
            Q11=makeQuery(id+"F27.boolean.opBoolean","COPY",EDGE,{"derivedFrom":makeQuery(id+"F27.opExtrude","SWEPT_EDGE",EDGE,{"disambiguationData":[OSD([sQuery(id+"F21.wireOp",EDGE,"E83.bottom"),sQuery(id+"F26.wireOp",EDGE,"E98.bottom"),sQuery(id+"F26.wireOp",EDGE,"E98.right")])]})});
            var Q12;
            Q12=makeQuery(id+"F27.boolean.opBoolean","COPY",EDGE,{"derivedFrom":makeQuery(id+"F27.opExtrude","SWEPT_EDGE",EDGE,{"disambiguationData":[OSD([sQuery(id+"F21.wireOp",EDGE,"E83.bottom"),sQuery(id+"F26.wireOp",EDGE,"E101.bottom"),sQuery(id+"F26.wireOp",EDGE,"E101.right")])]})});
            var Q13;
            Q13=makeQuery(id+"F27.boolean.opBoolean","COPY",EDGE,{"derivedFrom":makeQuery(id+"F27.opExtrude","SWEPT_EDGE",EDGE,{"disambiguationData":[OSD([sQuery(id+"F21.wireOp",EDGE,"E83.bottom"),sQuery(id+"F21.wireOp",EDGE,"E83.left"),sQuery(id+"F26.wireOp",EDGE,"E101.top"),sQuery(id+"F26.wireOp",EDGE,"E101.left")])]})});
            var Q14;
            Q14=makeQuery(id+"F27.boolean.opBoolean","COPY",EDGE,{"derivedFrom":makeQuery(id+"F27.opExtrude","SWEPT_EDGE",EDGE,{"disambiguationData":[OSD([sQuery(id+"F21.wireOp",EDGE,"E83.bottom"),sQuery(id+"F21.wireOp",EDGE,"E83.left"),sQuery(id+"F26.wireOp",EDGE,"E100.top"),sQuery(id+"F26.wireOp",EDGE,"E100.left")])]})});
            var Q15;
            Q15=makeQuery(id+"F27.boolean.opBoolean","COPY",EDGE,{"derivedFrom":makeQuery(id+"F27.opExtrude","SWEPT_EDGE",EDGE,{"disambiguationData":[OSD([sQuery(id+"F21.wireOp",EDGE,"E83.bottom"),sQuery(id+"F26.wireOp",EDGE,"E100.bottom"),sQuery(id+"F26.wireOp",EDGE,"E100.right")])]})});
            var Q16;
            Q16=makeQuery(id+"F27.boolean.opBoolean","COPY",EDGE,{"derivedFrom":makeQuery(id+"F27.opExtrude","SWEPT_EDGE",EDGE,{"disambiguationData":[OSD([sQuery(id+"F21.wireOp",EDGE,"E83.bottom"),sQuery(id+"F26.wireOp",EDGE,"E99.bottom"),sQuery(id+"F26.wireOp",EDGE,"E99.right")])]})});
            var Q17;
            Q17=makeQuery(id+"F27.boolean.opBoolean","COPY",EDGE,{"derivedFrom":makeQuery(id+"F27.opExtrude","SWEPT_EDGE",EDGE,{"disambiguationData":[OSD([sQuery(id+"F21.wireOp",EDGE,"E83.bottom"),sQuery(id+"F21.wireOp",EDGE,"E83.right"),sQuery(id+"F26.wireOp",EDGE,"E99.top"),sQuery(id+"F26.wireOp",EDGE,"E99.left")])]})});
            var Q18;
            Q18=makeQuery(id+"F27.boolean.opBoolean","COPY",EDGE,{"derivedFrom":makeQuery(id+"F27.opExtrude","CAP_EDGE",EDGE,{"disambiguationData":[OSD([sQuery(id+"F26.wireOp",EDGE,"E99.bottom")])],"isStart":false})});
            var Q19;
            Q19=makeQuery(id+"F22.opExtrude","CAP_EDGE",EDGE,{"disambiguationData":[OSD([sQuery(id+"F21.wireOp",EDGE,"E83.right")])],"isStart":false});
            var Q20;
            Q20=makeQuery(id+"F22.opExtrude","CAP_EDGE",EDGE,{"disambiguationData":[OSD([sQuery(id+"F21.wireOp",EDGE,"E83.top")])],"isStart":false});
            var Q21;
            {var subQ0=sQuery(id+"F21.wireOp",EDGE,"E83.left");var subQ1=sQuery(id+"F21.wireOp",EDGE,"E83.top");Q21=makeQuery(id+"F25.boolean.opBoolean","SPLIT",EDGE,{"disambiguationData":[TD([makeQuery(id+"F22.opExtrude","SWEPT_FACE",FACE,{"disambiguationData":[OSD([subQ1])]})])],"derivedFrom":makeQuery(id+"F22.opExtrude","CAP_EDGE",EDGE,{"disambiguationData":[OSD([subQ0])],"isStart":false})});}
            var Q22;
            {var subQ0=sQuery(id+"F21.wireOp",EDGE,"E83.left");var subQ1=sQuery(id+"F21.wireOp",EDGE,"E83.top");Q22=makeQuery(id+"F25.boolean.opBoolean","SPLIT",EDGE,{"disambiguationData":[TD([makeQuery(id+"F25.opExtrude","SWEPT_FACE",FACE,{"disambiguationData":[OSD([sQuery(id+"F24.wireOp",EDGE,"E96")])]})])],"derivedFrom":makeQuery(id+"F22.opExtrude","SWEPT_EDGE",EDGE,{"disambiguationData":[OSD([subQ1,subQ0])]})});}
            var Q23;
            {var subQ0=sQuery(id+"F21.wireOp",EDGE,"E83.left");var subQ1=sQuery(id+"F21.wireOp",EDGE,"E83.top");Q23=makeQuery(id+"F25.boolean.opBoolean","SPLIT",EDGE,{"disambiguationData":[TD([makeQuery(id+"F22.opExtrude","SWEPT_FACE",FACE,{"disambiguationData":[OSD([subQ1])]})])],"derivedFrom":makeQuery(id+"F22.opExtrude","CAP_EDGE",EDGE,{"disambiguationData":[OSD([subQ0])],"isStart":true})});}
            var Q24;
            {var subQ0=sQuery(id+"F21.wireOp",EDGE,"E83.left");var subQ1=sQuery(id+"F21.wireOp",EDGE,"E83.top");Q24=makeQuery(id+"F25.boolean.opBoolean","SPLIT",EDGE,{"disambiguationData":[TD([makeQuery(id+"F25.opExtrude","SWEPT_FACE",FACE,{"disambiguationData":[OSD([sQuery(id+"F24.wireOp",EDGE,"E94")])]})])],"derivedFrom":makeQuery(id+"F22.opExtrude","SWEPT_EDGE",EDGE,{"disambiguationData":[OSD([subQ1,subQ0])]})});}
            var Q25;
            Q25=makeQuery(id+"F22.opExtrude","CAP_EDGE",EDGE,{"disambiguationData":[OSD([sQuery(id+"F21.wireOp",EDGE,"E83.top")])],"isStart":true});
            var Q26;
            Q26=makeQuery(id+"F22.opExtrude","SWEPT_EDGE",EDGE,{"disambiguationData":[OSD([sQuery(id+"F21.wireOp",EDGE,"E83.top"),sQuery(id+"F21.wireOp",EDGE,"E83.right")])]});
            fillet(context, id + "F35", {"entities" : qUnion([Q0, Q1, Q2, Q3, Q4, Q5, Q6, Q7, Q8, Q9, Q10, Q11, Q12, Q13, Q14, Q15, Q16, Q17, Q18, Q19, Q20, Q21, Q22, Q23, Q24, Q25, Q26]), "radius" : 1 * mm, "tangentPropagation" : true, "allowEdgeOverflow" : false});
        }
        {
            var Q0;
            Q0=makeQuery(id+"F27.boolean.opBoolean","COPY",FACE,{"derivedFrom":makeQuery(id+"F27.opExtrude","CAP_FACE",FACE,{"disambiguationData":[OSD([sQuery(id+"F26.wireOp",EDGE,"E101.bottom"),sQuery(id+"F26.wireOp",EDGE,"E101.top"),sQuery(id+"F26.wireOp",EDGE,"E101.left"),sQuery(id+"F26.wireOp",EDGE,"E101.right")])],"isStart":false})});
            var sketch = newSketch(context, id + "F36", { "sketchPlane" : qUnion([Q0])});
            skLineSegment(sketch, "E123", {"start": v(-11.7, 9.05) * mm, "end": v(-17.7, 9.05) * mm});
            skLineSegment(sketch, "E124", {"start": v(-17.7, 9.05) * mm, "end": v(-17.7, 9.2) * mm});
            skLineSegment(sketch, "E125", {"start": v(-17.7, 9.2) * mm, "end": v(-23.7, 8.55) * mm});
            skLineSegment(sketch, "E126", {"start": v(-23.7, 8.55) * mm, "end": v(-23.7, 7.7) * mm});
            skLineSegment(sketch, "E127", {"start": v(-23.7, 7.7) * mm, "end": v(-11.7, 7.7) * mm});
            skLineSegment(sketch, "E128", {"start": v(-11.7, 7.7) * mm, "end": v(-11.7, 9.05) * mm});
            skLineSegment(sketch, "E129", {"start": v(-33.46, 6.05) * mm, "end": v(-12.91, 6.05) * mm, "construction": true});
            skSolve(sketch);
        }
        {
            var Q0;
            Q0=makeQuery(id+"F36.imprint","IMPRINT",FACE,{"disambiguationData":[TD([[makeQuery(id+"F36.imprint","IMPRINT",EDGE,{"derivedFrom":sQuery(id+"F36.wireOp",EDGE,"E123")}),1.0]])]});
            var Q1;
            Q1=sQuery(id+"F36.wireOp",EDGE,"E129");
            revolve(context, id + "F37", {"operationType" : NewBodyOperationType.ADD, "entities" : qUnion([Q0]), "axis" : qUnion([Q1]), "revolveType" : RevolveType.FULL});
        }
        {
            var Q0;
            Q0=makeQuery(id+"F37.opRevolve","SWEPT_EDGE",EDGE,{"disambiguationData":[OSD([sQuery(id+"F36.wireOp",EDGE,"E123"),sQuery(id+"F36.wireOp",EDGE,"E128")])]});
            fillet(context, id + "F38", {"entities" : qUnion([Q0]), "radius" : 1 * mm, "tangentPropagation" : true, "allowEdgeOverflow" : false});
        }
        {
            var Q0;
            Q0=makeQuery(id+"F19.opExtrude","SWEPT_FACE",FACE,{"disambiguationData":[OSD([sQuery(id+"F18.wireOp",EDGE,"E80.MirrorCS")])]});
            var sketch = newSketch(context, id + "F39", { "sketchPlane" : qUnion([Q0])});
            skCircle(sketch, "E130", {"center": v(-48.25, 23.75) * mm, "radius": 2.45 * mm});
            skCircle(sketch, "E131", {"center": v(-20.15, 23.75) * mm, "radius": 2.45 * mm});
            skCircle(sketch, "E132", {"center": v(-20.15, -23.75) * mm, "radius": 2.45 * mm});
            skCircle(sketch, "E133", {"center": v(-48.25, -23.75) * mm, "radius": 2.45 * mm});
            skLineSegment(sketch, "E134", {"start": v(-34.2, 28.2) * mm, "end": v(-34.2, -27.65) * mm, "construction": true});
            skSolve(sketch);
        }
        {
            var Q0;
            Q0=makeQuery(id+"F39.imprint","IMPRINT",FACE,{"disambiguationData":[TD([[makeQuery(id+"F39.imprint","IMPRINT",EDGE,{"derivedFrom":sQuery(id+"F39.wireOp",EDGE,"E130")}),1.0]])]});
            var Q1;
            Q1=makeQuery(id+"F39.imprint","IMPRINT",FACE,{"disambiguationData":[TD([[makeQuery(id+"F39.imprint","IMPRINT",EDGE,{"derivedFrom":sQuery(id+"F39.wireOp",EDGE,"E131")}),1.0]])]});
            var Q2;
            Q2=makeQuery(id+"F39.imprint","IMPRINT",FACE,{"disambiguationData":[TD([[makeQuery(id+"F39.imprint","IMPRINT",EDGE,{"derivedFrom":sQuery(id+"F39.wireOp",EDGE,"E132")}),1.0]])]});
            var Q3;
            Q3=makeQuery(id+"F39.imprint","IMPRINT",FACE,{"disambiguationData":[TD([[makeQuery(id+"F39.imprint","IMPRINT",EDGE,{"derivedFrom":sQuery(id+"F39.wireOp",EDGE,"E133")}),1.0]])]});
            extrude(context, id + "F40", {"entities" : qUnion([Q0, Q1, Q2, Q3]), "operationType" : NewBodyOperationType.REMOVE, "endBound" : BoundingType.UP_TO_NEXT, "oppositeDirection" : true, "depth" : 25 * mm});
        }
        {
            var Q0;
            Q0=makeQuery(id+"F19.opExtrude","SWEPT_FACE",FACE,{"disambiguationData":[OSD([sQuery(id+"F18.wireOp",EDGE,"E76")])]});
            var sketch = newSketch(context, id + "F41", { "sketchPlane" : qUnion([Q0])});
            skCircle(sketch, "E135", {"center": v(21.3, -20.69) * mm, "radius": 1.3 * mm});
            skCircle(sketch, "E136", {"center": v(47.1, -20.69) * mm, "radius": 1.3 * mm});
            skLineSegment(sketch, "E137", {"start": v(11.7, -20.69) * mm, "end": v(56.7, -20.69) * mm, "construction": true});
            skSolve(sketch);
        }
        {
            var Q0;
            Q0=makeQuery(id+"F41.imprint","IMPRINT",FACE,{"disambiguationData":[TD([[makeQuery(id+"F41.imprint","IMPRINT",EDGE,{"derivedFrom":sQuery(id+"F41.wireOp",EDGE,"E135")}),1.0]])]});
            var Q1;
            Q1=makeQuery(id+"F41.imprint","IMPRINT",FACE,{"disambiguationData":[TD([[makeQuery(id+"F41.imprint","IMPRINT",EDGE,{"derivedFrom":sQuery(id+"F41.wireOp",EDGE,"E136")}),1.0]])]});
            extrude(context, id + "F42", {"entities" : qUnion([Q0, Q1]), "operationType" : NewBodyOperationType.REMOVE, "endBound" : BoundingType.THROUGH_ALL, "oppositeDirection" : true, "depth" : 25 * mm});
        }
    });
